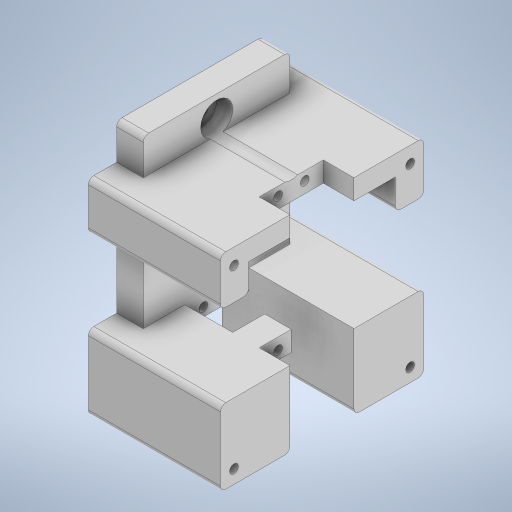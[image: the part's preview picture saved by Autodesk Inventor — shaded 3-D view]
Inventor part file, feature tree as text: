
AUTODESK INVENTOR PART (.ipt)
format: ipt  version: 2023 (Build 270158000, 158)  size: 479,232 bytes
history: native  units: in
note: dims shown in document units (in); Inventor stores cm internally (conversion verified against a paired STEP export)
features: extrude x8, sketch x5, fillet x2
ambient origin geometry x8: Origin, YZ Plane, XZ Plane, XY Plane, X Axis, Y Axis, Z Axis, Center Point
bodies: Solid1 (feature_tree)
feature tree (15):
  extrude  "Extrusion1"  Depth=2.1654in
  extrude  "Extrusion8"  Depth=1.1024in TaperAngle=0.0deg
  sketch  "Sketch10"  dims[d0=2.1654in d1=2.2441in]
  sketch  "Sketch14"  dims[d9=0.3937in d10=0.0in d63=1.1024in d64=0.0in]
  sketch  "Sketch15"  dims[d79=0.3937in d103=0.315in]
  extrude  "Extrusion17"  Depth=0.315in
  extrude  "Extrusion18"  Depth=0.4724in
  extrude  "Extrusion19"  Depth=0.4724in
  extrude  "Extrusion20"  Depth=3.0in
  extrude  "Extrusion21"  Depth=0.0787in
  extrude  "Extrusion23"  Depth=0.0787in
  fillet  "Fillet9"  Radius=0.3937in
  fillet  "Fillet10"  Radius=1.1811in
  sketch  "Sketch16"  dims[d104=1.0827in d108=0.4724in]
  sketch  "Sketch18"  dims[d109=0.4724in d112=0.4724in d121=3.0in d122=0.2756in d123=0.2756in d125=0.3937in d126=0.3937in d127=0.0in d128=0.0in d129=1.1811in d130=1.1909in d131=0.5118in d132=2.1654in d133=0.2362in d134=0.2362in d135=0.2362in d139=0.8268in d140=0.2953in d141=0.2953in d144=0.1299in d145=0.1299in d146=0.3937in d147=0.1673in d148=1.9685in d154=0.378in d162=0.378in d164=1.5in d165=0.2953in d166=0.378in d168=0.4173in d169=0.0in d170=0.6732in d171=1.5in d173=0.2953in d174=0.2953in d175=0.378in d176=0.2953in d177=0.4173in d178=0.4173in d179=0.2in d180=0.2in d181=0.2in d183=0.4528in d184=1.4961in d185=0.0in d186=0.0in d187=1.1024in d188=0.0in d189=1.3386in d190=0.0in d191=0.4724in d192=1.1024in d193=0.0in d197=0.3937in d198=0.4724in d199=0.3543in d200=0.0in d201=0.0787in d202=0.1299in d204=0.1673in d205=0.7874in d206=3.0in d208=0.2953in d209=0.2953in d210=0.0787in d194=0.0197in d195=0.0344in]
